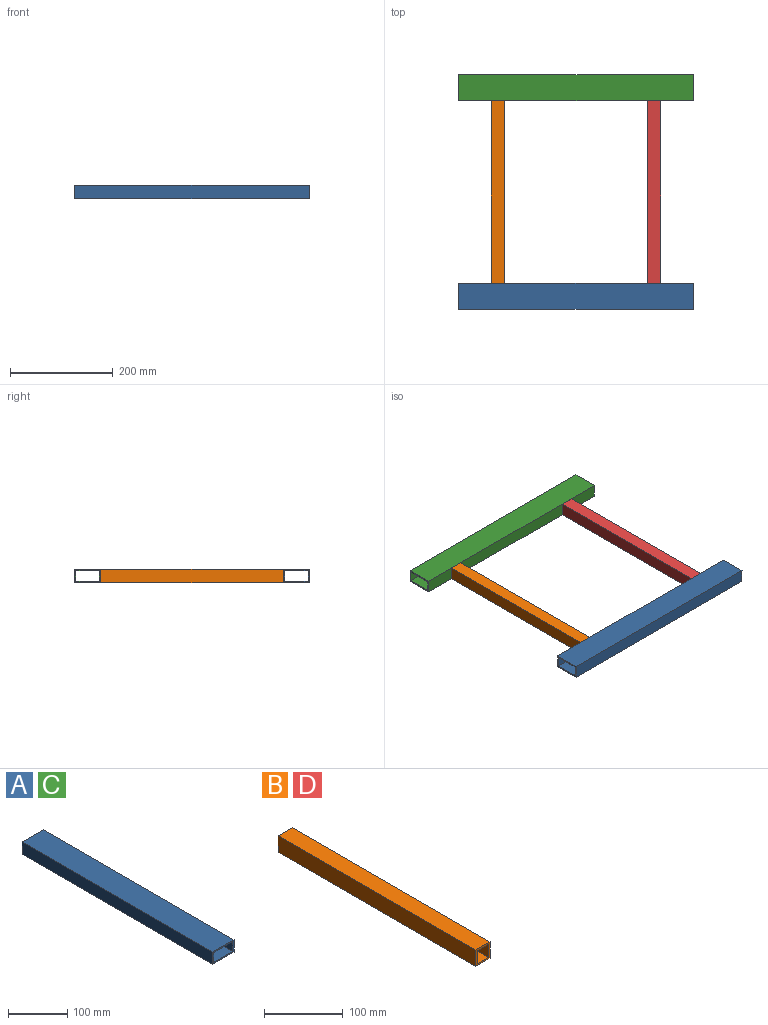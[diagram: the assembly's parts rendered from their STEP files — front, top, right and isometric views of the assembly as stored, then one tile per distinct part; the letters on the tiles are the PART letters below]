
ASSEMBLY  parts=4 mates=3
PART A: 10 faces, bbox 50.8x457.2x25.4 mm
  f0: plane 50.8x25.4mm, normal (0,1,0), area 361.3mm2, adj f2,f3,f4,f5,f6,f7,f8,f9
  f1: plane 50.8x25.4mm, normal (0,-1,0), area 361.3mm2, adj f2,f3,f4,f5,f6,f7,f8,f9
  f2: plane 457.2x25.4mm, normal (-1,0,0), area 11612.9mm2, adj f0,f1,f4,f5
  f3: plane 457.2x25.4mm, normal (1,0,0), area 11612.9mm2, adj f0,f1,f4,f5
  f4: plane 457.2x50.8mm, normal (0,0,1), area 23225.8mm2, adj f0,f1,f2,f3
  f5: plane 457.2x50.8mm, normal (0,0,-1), area 23225.8mm2, adj f0,f1,f2,f3
  f6: plane 457.2x20.32mm, normal (1,0,0), area 9290.3mm2, adj f0,f1,f8,f9
  f7: plane 457.2x20.32mm, normal (-1,0,0), area 9290.3mm2, adj f0,f1,f8,f9
  f8: plane 457.2x45.72mm, normal (0,0,-1), area 20903.2mm2, adj f0,f1,f6,f7
  f9: plane 457.2x45.72mm, normal (0,0,1), area 20903.2mm2, adj f0,f1,f6,f7
PART B: 10 faces, bbox 25.4x355.6x25.4 mm
  f0: plane 25.4x25.4mm, normal (0,1,0), area 232.3mm2, adj f2,f3,f4,f5,f6,f7,f8,f9
  f1: plane 25.4x25.4mm, normal (0,-1,0), area 232.3mm2, adj f2,f3,f4,f5,f6,f7,f8,f9
  f2: plane 355.6x25.4mm, normal (-1,0,0), area 9032.2mm2, adj f0,f1,f4,f5
  f3: plane 355.6x25.4mm, normal (1,0,0), area 9032.2mm2, adj f0,f1,f4,f5
  f4: plane 355.6x25.4mm, normal (0,0,1), area 9032.2mm2, adj f0,f1,f2,f3
  f5: plane 355.6x25.4mm, normal (0,0,-1), area 9032.2mm2, adj f0,f1,f2,f3
  f6: plane 355.6x20.32mm, normal (1,0,0), area 7225.8mm2, adj f0,f1,f8,f9
  f7: plane 355.6x20.32mm, normal (-1,0,0), area 7225.8mm2, adj f0,f1,f8,f9
  f8: plane 355.6x20.32mm, normal (0,0,-1), area 7225.8mm2, adj f0,f1,f6,f7
  f9: plane 355.6x20.32mm, normal (0,0,1), area 7225.8mm2, adj f0,f1,f6,f7
PART C: same geometry as A
PART D: same geometry as B
PLACE A rot(axis=(-0.71,-0.71,0),180deg) t=(568.73,-222.78,-5.6)mm
PLACE B rot(axis=(0,-1,0),90deg) t=(406.46,-23.07,148.32)mm
PLACE C rot(axis=(0,0,-1),90deg) t=(568.73,206.19,-5.6)mm
PLACE D rot(axis=(0.71,0,-0.71),180deg) t=(711.26,6.48,-159.52)mm
MATE fastened D.f0 <-> A.f3  axis (0,-1,0) through (711.26,-186.09,-5.6)mm
MATE fastened B.f1 <-> A.f3  axis (0,-1,0) through (406.46,-186.09,-5.6)mm
MATE fastened C.f3 <-> D.f1  axis (0,-1,0) through (711.26,169.51,-5.6)mm
